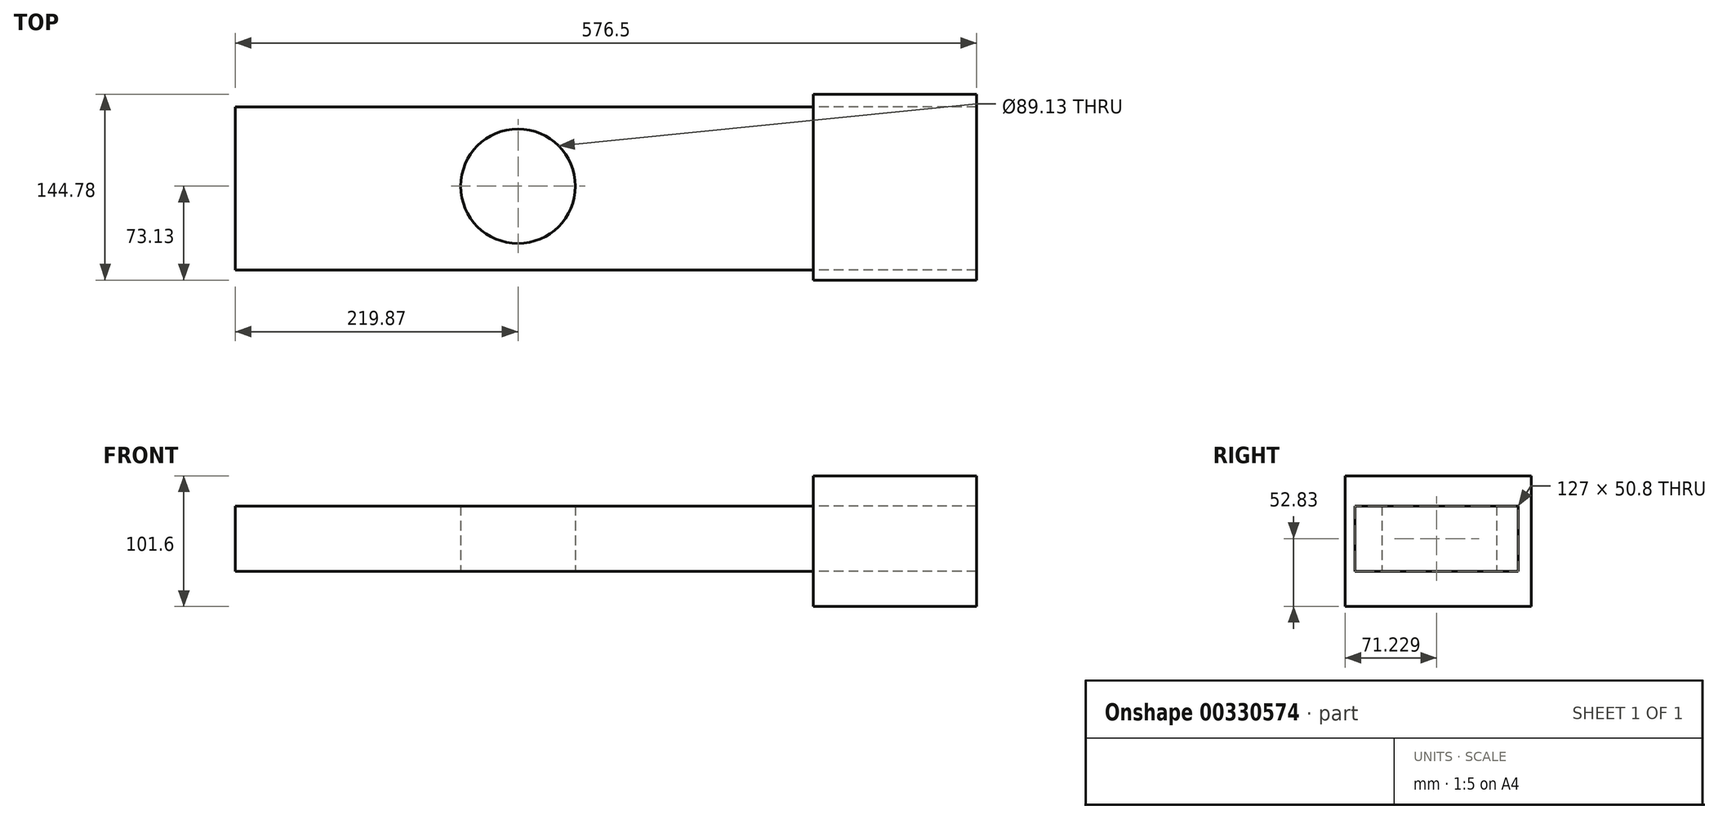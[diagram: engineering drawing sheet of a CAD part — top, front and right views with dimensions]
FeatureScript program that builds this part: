
annotation { "Feature Type Name" : "Feature", "Feature Type Description" : "" }
export const myFeature = defineFeature(function(context is Context, id is Id, definition is map)
    precondition{}
    {
        {
            var Q0;
            Q0=qCreatedBy(makeId("Top.planeOp"),FACE);
            var sketch = newSketch(context, id + "F0", { "sketchPlane" : qUnion([Q0])});
            skCircle(sketch, "E0", {"center": v(0, 0) * mm, "radius": 44.56 * mm});
            skLineSegment(sketch, "E1.bottom", {"start": v(-219.87, 61.6) * mm, "end": v(229.63, 61.6) * mm});
            skLineSegment(sketch, "E1.top", {"start": v(-219.87, -65.4) * mm, "end": v(229.63, -65.4) * mm});
            skLineSegment(sketch, "E1.left", {"start": v(-219.87, 61.6) * mm, "end": v(-219.87, -65.4) * mm});
            skLineSegment(sketch, "E1.right", {"start": v(229.63, 61.6) * mm, "end": v(229.63, -65.4) * mm});
            skSolve(sketch);
        }
        {
            var Q0;
            Q0 = qSketchRegion(id + "F0", true);
            extrude(context, id + "F1", {"entities" : qUnion([Q0]), "depth" : 50.8 * mm});
        }
        {
            var Q0;
            Q0=makeQuery(id+"F1.opExtrude","SWEPT_FACE",FACE,{"disambiguationData":[OSD([sQuery(id+"F0.wireOp",EDGE,"E1.right")])]});
            var sketch = newSketch(context, id + "F2", { "sketchPlane" : qUnion([Q0])});
            skLineSegment(sketch, "E2.bottom", {"start": v(-73.13, 74.17) * mm, "end": v(71.65, 74.17) * mm});
            skLineSegment(sketch, "E2.top", {"start": v(-73.13, -27.43) * mm, "end": v(71.65, -27.43) * mm});
            skLineSegment(sketch, "E2.left", {"start": v(-73.13, 74.17) * mm, "end": v(-73.13, -27.43) * mm});
            skLineSegment(sketch, "E2.right", {"start": v(71.65, 74.17) * mm, "end": v(71.65, -27.43) * mm});
            skSolve(sketch);
        }
        {
            var Q0;
            Q0=makeQuery(id+"F2.imprint","IMPRINT",FACE,{"disambiguationData":[TD([[makeQuery(id+"F2.imprint","IMPRINT",EDGE,{"derivedFrom":sQuery(id+"F2.wireOp",EDGE,"E2.bottom")}),-1.0]])]});
            extrude(context, id + "F3", {"entities" : qUnion([Q0]), "depth" : 127 * mm});
        }
    });
